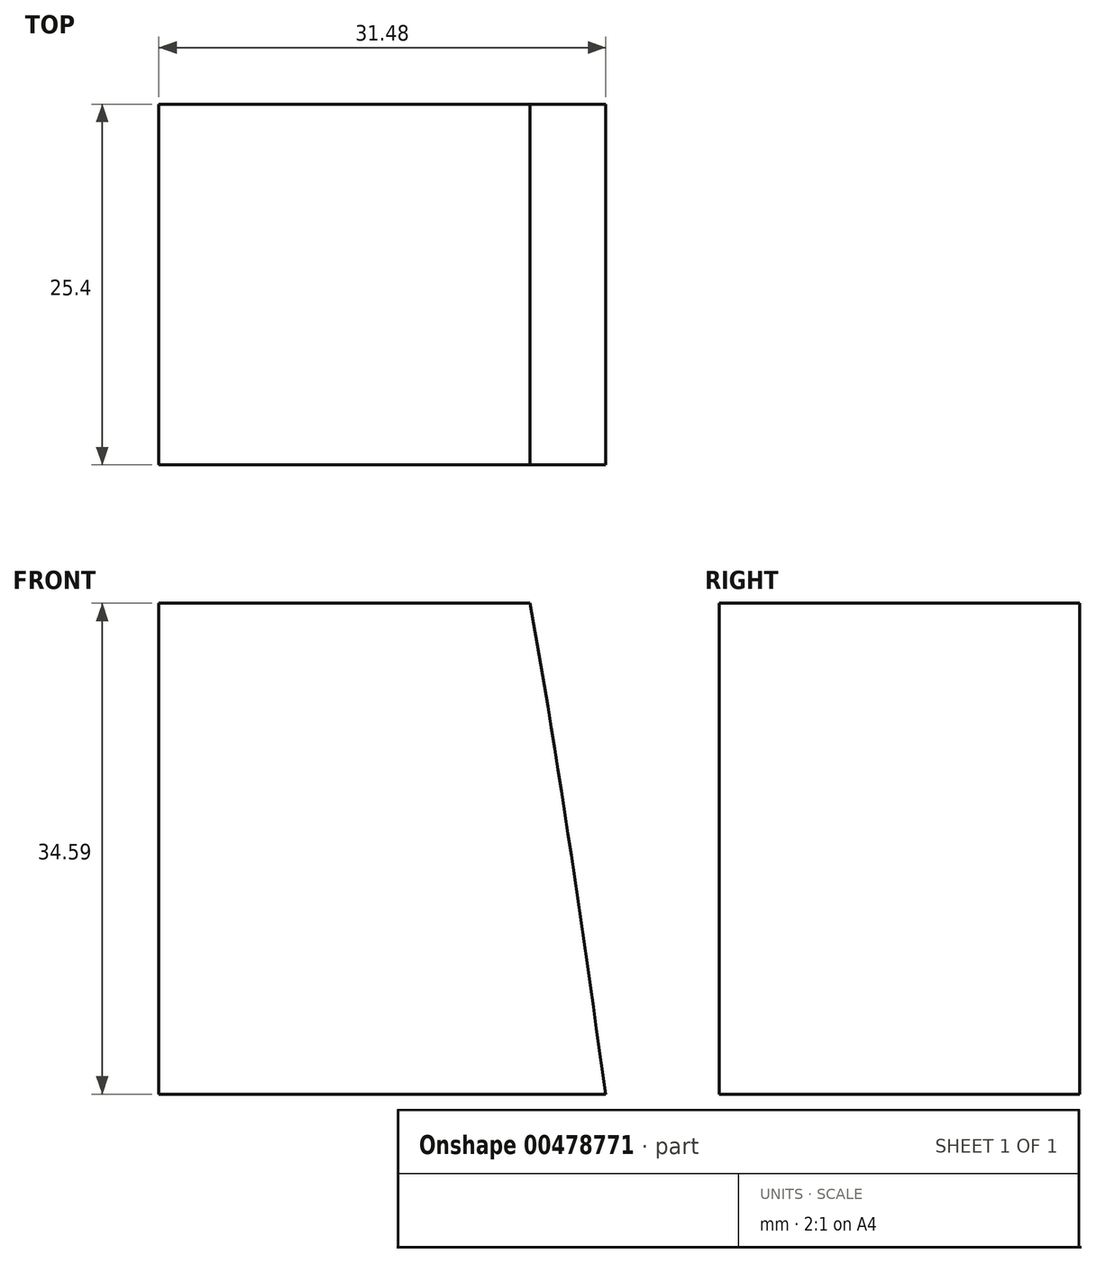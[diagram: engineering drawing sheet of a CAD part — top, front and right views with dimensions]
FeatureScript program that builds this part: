
annotation { "Feature Type Name" : "Feature", "Feature Type Description" : "" }
export const myFeature = defineFeature(function(context is Context, id is Id, definition is map)
    precondition{}
    {
        {
            var Q0;
            Q0=qCreatedBy(makeId("Front.planeOp"),FACE);
            var sketch = newSketch(context, id + "F0", { "sketchPlane" : qUnion([Q0])});
            skLineSegment(sketch, "E0.bottom", {"start": v(63.5, 34.42) * mm, "end": v(-63.5, 34.42) * mm});
            skLineSegment(sketch, "E0.top", {"start": v(63.5, -34.42) * mm, "end": v(-63.5, -34.42) * mm});
            skLineSegment(sketch, "E0.left", {"start": v(63.5, 34.42) * mm, "end": v(63.5, -34.42) * mm});
            skLineSegment(sketch, "E0.right", {"start": v(-63.5, 34.42) * mm, "end": v(-63.5, -34.42) * mm});
            skPoint(sketch, "E0.middle", {"position": v(0, 0) * mm});
            skLineSegment(sketch, "E1.bottom", {"start": v(32.02, 13.51) * mm, "end": v(168.62, 13.51) * mm});
            skLineSegment(sketch, "E1.top", {"start": v(32.02, 124.5) * mm, "end": v(168.62, 124.5) * mm});
            skLineSegment(sketch, "E1.left", {"start": v(32.02, 13.51) * mm, "end": v(32.02, 124.5) * mm});
            skLineSegment(sketch, "E1.right", {"start": v(168.62, 13.51) * mm, "end": v(168.62, 124.5) * mm});
            skPoint(sketch, "E1.middle", {"position": v(100.32, 69.01) * mm});
            skLineSegment(sketch, "E2.bottom", {"start": v(-63.5, 71.77) * mm, "end": v(-63.5, 71.77) * mm});
            skLineSegment(sketch, "E2.top", {"start": v(-63.5, -2.93) * mm, "end": v(-63.5, -2.93) * mm});
            skLineSegment(sketch, "E2.left", {"start": v(-63.5, 71.77) * mm, "end": v(-63.5, -2.93) * mm});
            skLineSegment(sketch, "E2.right", {"start": v(-63.5, 71.77) * mm, "end": v(-63.5, -2.93) * mm});
            skPoint(sketch, "E2.middle", {"position": v(-63.5, 34.42) * mm});
            skLineSegment(sketch, "E3", {"start": v(-63.54, 71.74) * mm, "end": v(-63.5, 71.77) * mm});
            skArc(sketch, "E4", {"start": v(-63.54, 71.74) * mm, "mid": v(-31.19, 83.88) * mm, "end": v(0, 69.01) * mm});
            skLineSegment(sketch, "E5", {"start": v(0, 69.01) * mm, "end": v(100.32, 69.01) * mm});
            skLineSegment(sketch, "E6.0", {"start": v(14.15, 107.11) * mm, "end": v(93.24, 107.11) * mm});
            skArc(sketch, "E6.1", {"start": v(-89.81, 99.33) * mm, "mid": v(-39.22, 121.79) * mm, "end": v(14.15, 107.11) * mm});
            skLineSegment(sketch, "E6.2", {"start": v(-90.5, 98.66) * mm, "end": v(-89.81, 99.33) * mm});
            skLineSegment(sketch, "E7", {"start": v(-90.5, 98.66) * mm, "end": v(-90.5, 34.8) * mm});
            skLineSegment(sketch, "E8", {"start": v(-63.5, 34.42) * mm, "end": v(-90.5, 34.42) * mm});
            skLineSegment(sketch, "E9", {"start": v(93.24, 107.11) * mm, "end": v(100.32, 69.01) * mm});
            skFitSpline(sketch, "E10", {"points": [v(-63.5, 71.77) * mm, v(32.02, 124.5) * mm, v(63.5, 34.42) * mm], "startDerivative": vector(215.77, 176.59) * mm, "endDerivative": vector(36.22, -256.12) * mm});
            skSolve(sketch);
        }
        {
            var Q0;
            {var subQ5=sQuery(id+"F0.wireOp",EDGE,"E2.right");var subQ6=sQuery(id+"F0.wireOp",EDGE,"E0.bottom");var subQ7=makeQuery(id+"F0.imprint","INTERSECT",VERTEX,{"derivedFrom":[subQ6,subQ5]});Q0=makeQuery(id+"F0.imprint","IMPRINT",FACE,{"disambiguationData":[TD([[makeQuery(id+"F0.imprint","IMPRINT",EDGE,{"disambiguationData":[TD([[subQ7,1.0]])],"derivedFrom":subQ6}),-1.0]])]});}
            extrude(context, id + "F1", {"entities" : qUnion([Q0]), "endBound" : BoundingType.SYMMETRIC, "depth" : 25.4 * mm});
        }
    });
